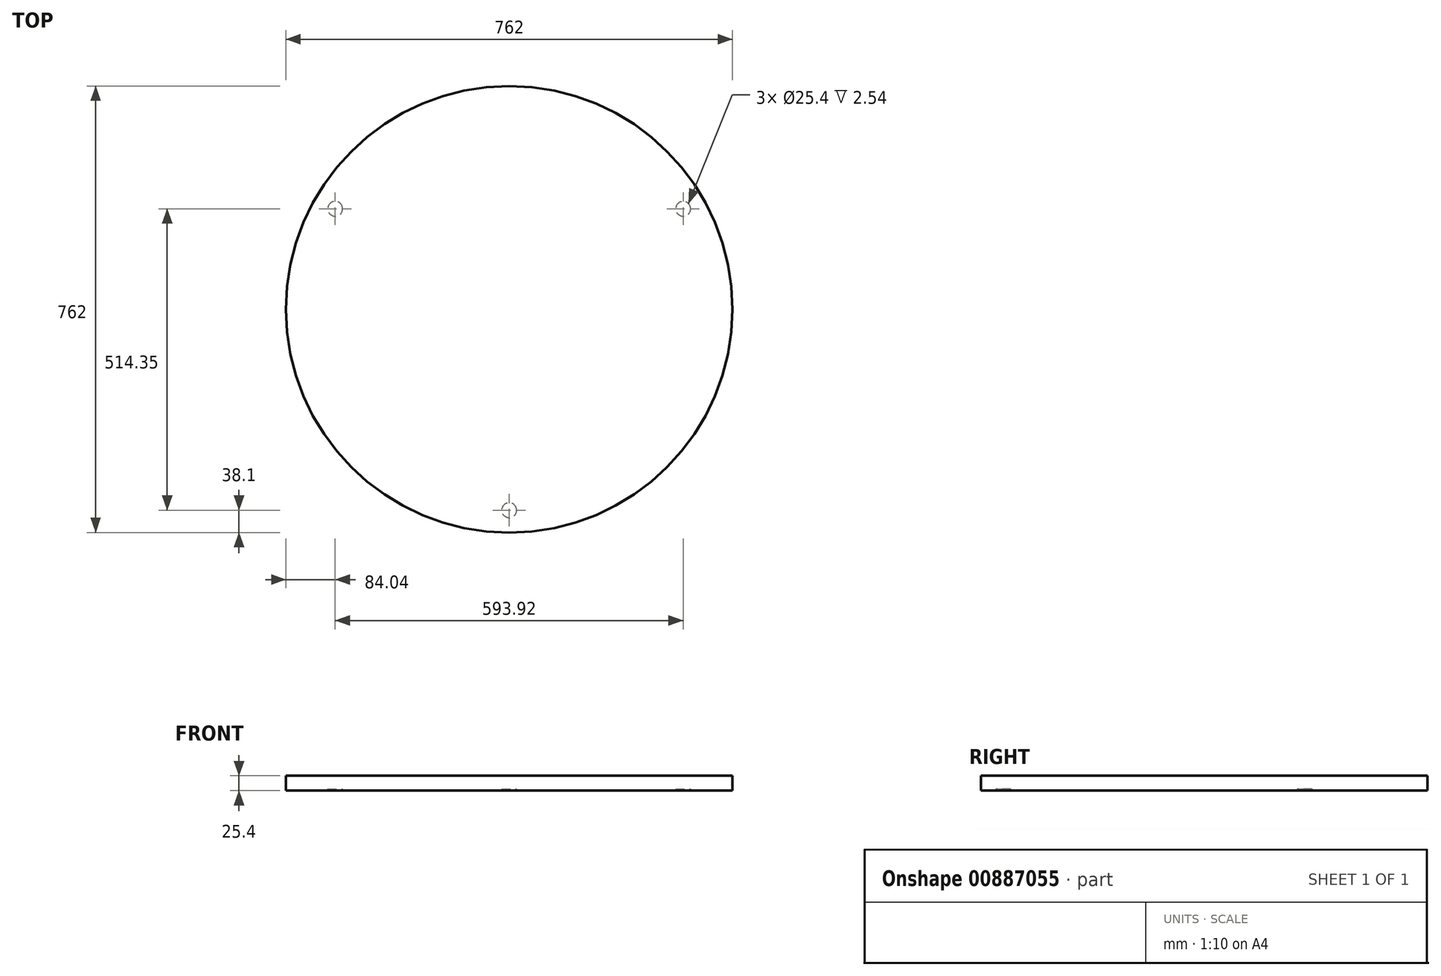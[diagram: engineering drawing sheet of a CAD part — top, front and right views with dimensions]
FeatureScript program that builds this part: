
annotation { "Feature Type Name" : "Feature", "Feature Type Description" : "" }
export const myFeature = defineFeature(function(context is Context, id is Id, definition is map)
    precondition{}
    {
        {
            var Q0;
            Q0=qCreatedBy(makeId("Top.planeOp"),FACE);
            var sketch = newSketch(context, id + "F0", { "sketchPlane" : qUnion([Q0])});
            skCircle(sketch, "E0", {"center": v(0, 0) * mm, "radius": 381 * mm});
            skSolve(sketch);
        }
        {
            var Q0;
            Q0=makeQuery(id+"F0.imprint","IMPRINT",FACE,{"disambiguationData":[TD([[makeQuery(id+"F0.imprint","IMPRINT",EDGE,{"derivedFrom":sQuery(id+"F0.wireOp",EDGE,"E0")}),1.0]])]});
            extrude(context, id + "F1", {"entities" : qUnion([Q0]), "depth" : 25.4 * mm, "offsetDistance" : 25.4 * mm});
        }
        {
            var Q0;
            Q0=makeQuery(id+"F1.opExtrude","CAP_FACE",FACE,{"disambiguationData":[OSD([sQuery(id+"F0.wireOp",EDGE,"E0")])],"isStart":true});
            var sketch = newSketch(context, id + "F2", { "sketchPlane" : qUnion([Q0])});
            skPoint(sketch, "E1.middle", {"position": v(0, 0) * mm});
            skCircle(sketch, "E2", {"center": v(0, 0) * mm, "radius": 685.8 * mm, "construction": true});
            skLineSegment(sketch, "E3.0", {"start": v(0, -685.8) * mm, "end": v(-593.92, 342.9) * mm, "construction": true});
            skLineSegment(sketch, "E3.1", {"start": v(-593.92, 342.9) * mm, "end": v(593.92, 342.9) * mm, "construction": true});
            skLineSegment(sketch, "E3.2", {"start": v(593.92, 342.9) * mm, "end": v(0, -685.8) * mm, "construction": true});
            skCircle(sketch, "E4", {"center": v(-296.96, -171.45) * mm, "radius": 12.7 * mm});
            skCircle(sketch, "E5", {"center": v(296.96, -171.45) * mm, "radius": 12.7 * mm});
            skCircle(sketch, "E6", {"center": v(0, 342.9) * mm, "radius": 12.7 * mm});
            skSolve(sketch);
        }
        {
            var Q0;
            Q0=makeQuery(id+"F2.imprint","IMPRINT",FACE,{"disambiguationData":[TD([[makeQuery(id+"F2.imprint","IMPRINT",EDGE,{"derivedFrom":sQuery(id+"F2.wireOp",EDGE,"E6")}),1.0]])]});
            var Q1;
            Q1=makeQuery(id+"F2.imprint","IMPRINT",FACE,{"disambiguationData":[TD([[makeQuery(id+"F2.imprint","IMPRINT",EDGE,{"derivedFrom":sQuery(id+"F2.wireOp",EDGE,"E4")}),1.0]])]});
            var Q2;
            Q2=makeQuery(id+"F2.imprint","IMPRINT",FACE,{"disambiguationData":[TD([[makeQuery(id+"F2.imprint","IMPRINT",EDGE,{"derivedFrom":sQuery(id+"F2.wireOp",EDGE,"E5")}),1.0]])]});
            extrude(context, id + "F3", {"entities" : qUnion([Q0, Q1, Q2]), "operationType" : NewBodyOperationType.REMOVE, "oppositeDirection" : true, "depth" : 2.54 * mm, "offsetDistance" : 25.4 * mm});
        }
    });
